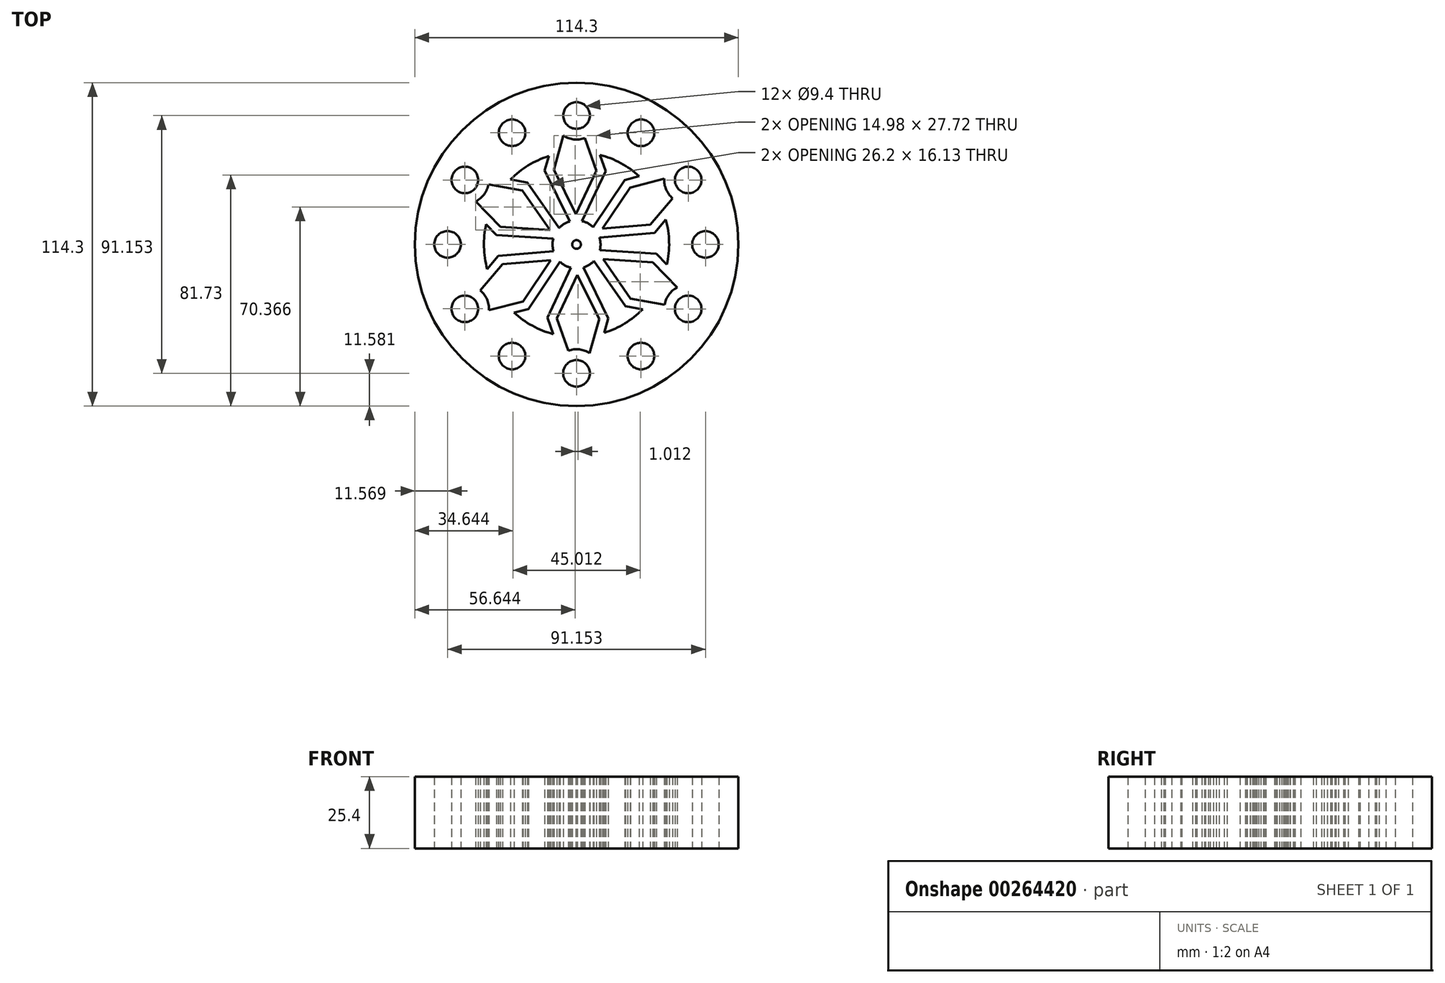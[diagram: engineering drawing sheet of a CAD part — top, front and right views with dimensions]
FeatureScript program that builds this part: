
annotation { "Feature Type Name" : "Feature", "Feature Type Description" : "" }
export const myFeature = defineFeature(function(context is Context, id is Id, definition is map)
    precondition{}
    {
        {
            var Q0;
            Q0=qCreatedBy(makeId("Top.planeOp"),FACE);
            var sketch = newSketch(context, id + "F0", { "sketchPlane" : qUnion([Q0])});
            skCircle(sketch, "E0", {"center": v(0, 0) * mm, "radius": 57.15 * mm});
            skCircle(sketch, "E1", {"center": v(45.57, 0) * mm, "radius": 4.7 * mm});
            skCircle(sketch, "E2.1.0", {"center": v(39.47, 22.79) * mm, "radius": 4.7 * mm});
            skCircle(sketch, "E2.2.0", {"center": v(22.8, 39.47) * mm, "radius": 4.7 * mm});
            skCircle(sketch, "E2.3.0", {"center": v(0, 45.58) * mm, "radius": 4.7 * mm});
            skCircle(sketch, "E2.4.0", {"center": v(-22.79, 39.48) * mm, "radius": 4.7 * mm});
            skCircle(sketch, "E2.5.0", {"center": v(-39.47, 22.8) * mm, "radius": 4.7 * mm});
            skCircle(sketch, "E2.6.0", {"center": v(-45.58, 0.02) * mm, "radius": 4.7 * mm});
            skCircle(sketch, "E2.7.0", {"center": v(-39.48, -22.77) * mm, "radius": 4.7 * mm});
            skCircle(sketch, "E2.8.0", {"center": v(-22.8, -39.46) * mm, "radius": 4.7 * mm});
            skCircle(sketch, "E2.9.0", {"center": v(-0.01, -45.57) * mm, "radius": 4.7 * mm});
            skCircle(sketch, "E2.10.0", {"center": v(22.78, -39.47) * mm, "radius": 4.7 * mm});
            skCircle(sketch, "E2.11.0", {"center": v(39.46, -22.79) * mm, "radius": 4.7 * mm});
            skCircle(sketch, "E3", {"center": v(0, 0) * mm, "radius": 1.52 * mm});
            skPoint(sketch, "E4.start.orphan", {"position": v(10.09, 0) * mm});
            skPoint(sketch, "E5.0.internal.orphan", {"position": v(0, 10.09) * mm});
            skArc(sketch, "E6", {"start": v(8.24, -2.02) * mm, "mid": v(8.48, 0.2) * mm, "end": v(8.13, 2.42) * mm});
            skArc(sketch, "E7", {"start": v(31.95, -7.1) * mm, "mid": v(32.72, 0.83) * mm, "end": v(31.55, 8.72) * mm});
            skLineSegment(sketch, "E8", {"start": v(8.13, 2.42) * mm, "end": v(27.6, 4.07) * mm});
            skLineSegment(sketch, "E9", {"start": v(27.6, 4.07) * mm, "end": v(31.55, 8.72) * mm});
            skLineSegment(sketch, "E10", {"start": v(8.24, -2.02) * mm, "end": v(28.26, -3.33) * mm});
            skLineSegment(sketch, "E11", {"start": v(28.26, -3.33) * mm, "end": v(31.95, -7.1) * mm});
            skLineSegment(sketch, "E12.1.0", {"start": v(5.87, 6.12) * mm, "end": v(17, 22.8) * mm});
            skPoint(sketch, "E12.1.1", {"position": v(5.04, 8.73) * mm});
            skLineSegment(sketch, "E12.1.2", {"start": v(1.97, 8.25) * mm, "end": v(10.28, 25.94) * mm});
            skLineSegment(sketch, "E12.1.3", {"start": v(17, 22.8) * mm, "end": v(22.13, 24.12) * mm});
            skLineSegment(sketch, "E12.1.4", {"start": v(10.28, 25.94) * mm, "end": v(8.23, 31.68) * mm});
            skArc(sketch, "E12.1.5", {"start": v(22.13, 24.12) * mm, "mid": v(15.64, 28.75) * mm, "end": v(8.23, 31.68) * mm});
            skArc(sketch, "E12.1.6", {"start": v(5.87, 6.12) * mm, "mid": v(4.06, 7.45) * mm, "end": v(1.97, 8.25) * mm});
            skLineSegment(sketch, "E12.2.0", {"start": v(-2.37, 8.14) * mm, "end": v(-11.25, 26.13) * mm});
            skPoint(sketch, "E12.2.1", {"position": v(-5.04, 8.73) * mm});
            skLineSegment(sketch, "E12.2.2", {"start": v(-6.16, 5.83) * mm, "end": v(-17.33, 21.87) * mm});
            skLineSegment(sketch, "E12.2.3", {"start": v(-11.25, 26.13) * mm, "end": v(-9.82, 31.22) * mm});
            skLineSegment(sketch, "E12.2.4", {"start": v(-17.33, 21.87) * mm, "end": v(-23.32, 22.96) * mm});
            skArc(sketch, "E12.2.5", {"start": v(-9.82, 31.22) * mm, "mid": v(-17.08, 27.92) * mm, "end": v(-23.32, 22.96) * mm});
            skArc(sketch, "E12.2.6", {"start": v(-2.37, 8.14) * mm, "mid": v(-4.42, 7.24) * mm, "end": v(-6.16, 5.83) * mm});
            skLineSegment(sketch, "E12.3.0", {"start": v(-8.24, 2.02) * mm, "end": v(-28.26, 3.33) * mm});
            skPoint(sketch, "E12.3.1", {"position": v(-10.09, 0) * mm});
            skLineSegment(sketch, "E12.3.2", {"start": v(-8.13, -2.42) * mm, "end": v(-27.6, -4.07) * mm});
            skLineSegment(sketch, "E12.3.3", {"start": v(-28.26, 3.33) * mm, "end": v(-31.95, 7.1) * mm});
            skLineSegment(sketch, "E12.3.4", {"start": v(-27.6, -4.07) * mm, "end": v(-31.55, -8.72) * mm});
            skArc(sketch, "E12.3.5", {"start": v(-31.95, 7.1) * mm, "mid": v(-32.72, -0.83) * mm, "end": v(-31.55, -8.72) * mm});
            skArc(sketch, "E12.3.6", {"start": v(-8.24, 2.02) * mm, "mid": v(-8.48, -0.2) * mm, "end": v(-8.13, -2.42) * mm});
            skLineSegment(sketch, "E12.4.0", {"start": v(-5.87, -6.12) * mm, "end": v(-17, -22.8) * mm});
            skPoint(sketch, "E12.4.1", {"position": v(-5.04, -8.73) * mm});
            skLineSegment(sketch, "E12.4.2", {"start": v(-1.97, -8.25) * mm, "end": v(-10.28, -25.94) * mm});
            skLineSegment(sketch, "E12.4.3", {"start": v(-17, -22.8) * mm, "end": v(-22.13, -24.12) * mm});
            skLineSegment(sketch, "E12.4.4", {"start": v(-10.28, -25.94) * mm, "end": v(-8.23, -31.68) * mm});
            skArc(sketch, "E12.4.5", {"start": v(-22.13, -24.12) * mm, "mid": v(-15.64, -28.75) * mm, "end": v(-8.23, -31.68) * mm});
            skArc(sketch, "E12.4.6", {"start": v(-5.87, -6.12) * mm, "mid": v(-4.06, -7.45) * mm, "end": v(-1.97, -8.25) * mm});
            skLineSegment(sketch, "E12.5.0", {"start": v(2.37, -8.14) * mm, "end": v(11.25, -26.13) * mm});
            skPoint(sketch, "E12.5.1", {"position": v(5.04, -8.73) * mm});
            skLineSegment(sketch, "E12.5.2", {"start": v(6.16, -5.83) * mm, "end": v(17.33, -21.87) * mm});
            skLineSegment(sketch, "E12.5.3", {"start": v(11.25, -26.13) * mm, "end": v(9.82, -31.22) * mm});
            skLineSegment(sketch, "E12.5.4", {"start": v(17.33, -21.87) * mm, "end": v(23.32, -22.96) * mm});
            skArc(sketch, "E12.5.5", {"start": v(9.82, -31.22) * mm, "mid": v(17.08, -27.92) * mm, "end": v(23.32, -22.96) * mm});
            skArc(sketch, "E12.5.6", {"start": v(2.37, -8.14) * mm, "mid": v(4.42, -7.24) * mm, "end": v(6.16, -5.83) * mm});
            skLineSegment(sketch, "E13.0", {"start": v(18.9, 20.14) * mm, "end": v(22.88, 21.16) * mm});
            skLineSegment(sketch, "E13.1", {"start": v(9.16, 5.57) * mm, "end": v(18.9, 20.14) * mm});
            skLineSegment(sketch, "E14.0", {"start": v(26.1, 7) * mm, "end": v(29.22, 10.69) * mm});
            skLineSegment(sketch, "E14.1", {"start": v(9.16, 5.57) * mm, "end": v(26.1, 7) * mm});
            skLineSegment(sketch, "E15", {"start": v(22.88, 21.16) * mm, "end": v(29.35, 22.82) * mm});
            skLineSegment(sketch, "E16", {"start": v(29.22, 10.69) * mm, "end": v(33.62, 15.87) * mm});
            skArc(sketch, "E17.0", {"start": v(30.97, 23.24) * mm, "mid": v(31.66, 19.41) * mm, "end": v(33.98, 16.3) * mm});
            skLineSegment(sketch, "E18", {"start": v(29.35, 22.82) * mm, "end": v(30.97, 23.24) * mm});
            skLineSegment(sketch, "E19", {"start": v(33.62, 15.87) * mm, "end": v(33.98, 16.3) * mm});
            skLineSegment(sketch, "E20.1.0", {"start": v(-8, 26.44) * mm, "end": v(-6.89, 30.4) * mm});
            skLineSegment(sketch, "E20.1.1", {"start": v(-6.89, 30.4) * mm, "end": v(-5.09, 36.83) * mm});
            skLineSegment(sketch, "E20.1.2", {"start": v(-5.09, 36.83) * mm, "end": v(-4.64, 38.44) * mm});
            skArc(sketch, "E20.1.3", {"start": v(-4.64, 38.44) * mm, "mid": v(-0.98, 37.12) * mm, "end": v(2.88, 37.57) * mm});
            skLineSegment(sketch, "E20.1.4", {"start": v(5.36, 30.65) * mm, "end": v(3.07, 37.05) * mm});
            skLineSegment(sketch, "E20.1.5", {"start": v(6.98, 26.1) * mm, "end": v(5.36, 30.65) * mm});
            skLineSegment(sketch, "E20.1.6", {"start": v(-0.24, 10.72) * mm, "end": v(6.98, 26.1) * mm});
            skLineSegment(sketch, "E20.1.7", {"start": v(-0.24, 10.72) * mm, "end": v(-8, 26.44) * mm});
            skLineSegment(sketch, "E20.1.8", {"start": v(3.07, 37.05) * mm, "end": v(2.88, 37.57) * mm});
            skLineSegment(sketch, "E20.2.0", {"start": v(-26.9, 6.3) * mm, "end": v(-29.77, 9.24) * mm});
            skLineSegment(sketch, "E20.2.1", {"start": v(-29.77, 9.24) * mm, "end": v(-34.44, 14) * mm});
            skLineSegment(sketch, "E20.2.2", {"start": v(-34.44, 14) * mm, "end": v(-35.6, 15.2) * mm});
            skArc(sketch, "E20.2.3", {"start": v(-35.6, 15.2) * mm, "mid": v(-32.64, 17.71) * mm, "end": v(-31.1, 21.28) * mm});
            skLineSegment(sketch, "E20.2.4", {"start": v(-23.87, 19.96) * mm, "end": v(-30.55, 21.18) * mm});
            skLineSegment(sketch, "E20.2.5", {"start": v(-19.11, 19.1) * mm, "end": v(-23.87, 19.96) * mm});
            skLineSegment(sketch, "E20.2.6", {"start": v(-9.4, 5.15) * mm, "end": v(-19.11, 19.1) * mm});
            skLineSegment(sketch, "E20.2.7", {"start": v(-9.4, 5.15) * mm, "end": v(-26.9, 6.3) * mm});
            skLineSegment(sketch, "E20.2.8", {"start": v(-30.55, 21.18) * mm, "end": v(-31.1, 21.28) * mm});
            skLineSegment(sketch, "E20.3.0", {"start": v(-18.9, -20.14) * mm, "end": v(-22.88, -21.16) * mm});
            skLineSegment(sketch, "E20.3.1", {"start": v(-22.88, -21.16) * mm, "end": v(-29.35, -22.82) * mm});
            skLineSegment(sketch, "E20.3.2", {"start": v(-29.35, -22.82) * mm, "end": v(-30.97, -23.24) * mm});
            skArc(sketch, "E20.3.3", {"start": v(-30.97, -23.24) * mm, "mid": v(-31.66, -19.41) * mm, "end": v(-33.98, -16.3) * mm});
            skLineSegment(sketch, "E20.3.4", {"start": v(-29.22, -10.69) * mm, "end": v(-33.62, -15.87) * mm});
            skLineSegment(sketch, "E20.3.5", {"start": v(-26.1, -7) * mm, "end": v(-29.22, -10.69) * mm});
            skLineSegment(sketch, "E20.3.6", {"start": v(-9.16, -5.57) * mm, "end": v(-26.1, -7) * mm});
            skLineSegment(sketch, "E20.3.7", {"start": v(-9.16, -5.57) * mm, "end": v(-18.9, -20.14) * mm});
            skLineSegment(sketch, "E20.3.8", {"start": v(-33.62, -15.87) * mm, "end": v(-33.98, -16.3) * mm});
            skLineSegment(sketch, "E20.4.0", {"start": v(8, -26.44) * mm, "end": v(6.89, -30.4) * mm});
            skLineSegment(sketch, "E20.4.1", {"start": v(6.89, -30.4) * mm, "end": v(5.09, -36.83) * mm});
            skLineSegment(sketch, "E20.4.2", {"start": v(5.09, -36.83) * mm, "end": v(4.64, -38.44) * mm});
            skArc(sketch, "E20.4.3", {"start": v(4.64, -38.44) * mm, "mid": v(0.98, -37.12) * mm, "end": v(-2.88, -37.57) * mm});
            skLineSegment(sketch, "E20.4.4", {"start": v(-5.36, -30.65) * mm, "end": v(-3.07, -37.05) * mm});
            skLineSegment(sketch, "E20.4.5", {"start": v(-6.98, -26.1) * mm, "end": v(-5.36, -30.65) * mm});
            skLineSegment(sketch, "E20.4.6", {"start": v(0.24, -10.72) * mm, "end": v(-6.98, -26.1) * mm});
            skLineSegment(sketch, "E20.4.7", {"start": v(0.24, -10.72) * mm, "end": v(8, -26.44) * mm});
            skLineSegment(sketch, "E20.4.8", {"start": v(-3.07, -37.05) * mm, "end": v(-2.88, -37.57) * mm});
            skLineSegment(sketch, "E20.5.0", {"start": v(26.9, -6.3) * mm, "end": v(29.77, -9.24) * mm});
            skLineSegment(sketch, "E20.5.1", {"start": v(29.77, -9.24) * mm, "end": v(34.44, -14) * mm});
            skLineSegment(sketch, "E20.5.2", {"start": v(34.44, -14) * mm, "end": v(35.6, -15.2) * mm});
            skArc(sketch, "E20.5.3", {"start": v(35.6, -15.2) * mm, "mid": v(32.64, -17.71) * mm, "end": v(31.1, -21.28) * mm});
            skLineSegment(sketch, "E20.5.4", {"start": v(23.87, -19.96) * mm, "end": v(30.55, -21.18) * mm});
            skLineSegment(sketch, "E20.5.5", {"start": v(19.11, -19.1) * mm, "end": v(23.87, -19.96) * mm});
            skLineSegment(sketch, "E20.5.6", {"start": v(9.4, -5.15) * mm, "end": v(19.11, -19.1) * mm});
            skLineSegment(sketch, "E20.5.7", {"start": v(9.4, -5.15) * mm, "end": v(26.9, -6.3) * mm});
            skLineSegment(sketch, "E20.5.8", {"start": v(30.55, -21.18) * mm, "end": v(31.1, -21.28) * mm});
            skSolve(sketch);
        }
        {
            var Q0;
            Q0 = qSketchRegion(id + "F0", true);
            extrude(context, id + "F1", {"entities" : qUnion([Q0]), "depth" : 25.4 * mm});
        }
    });
